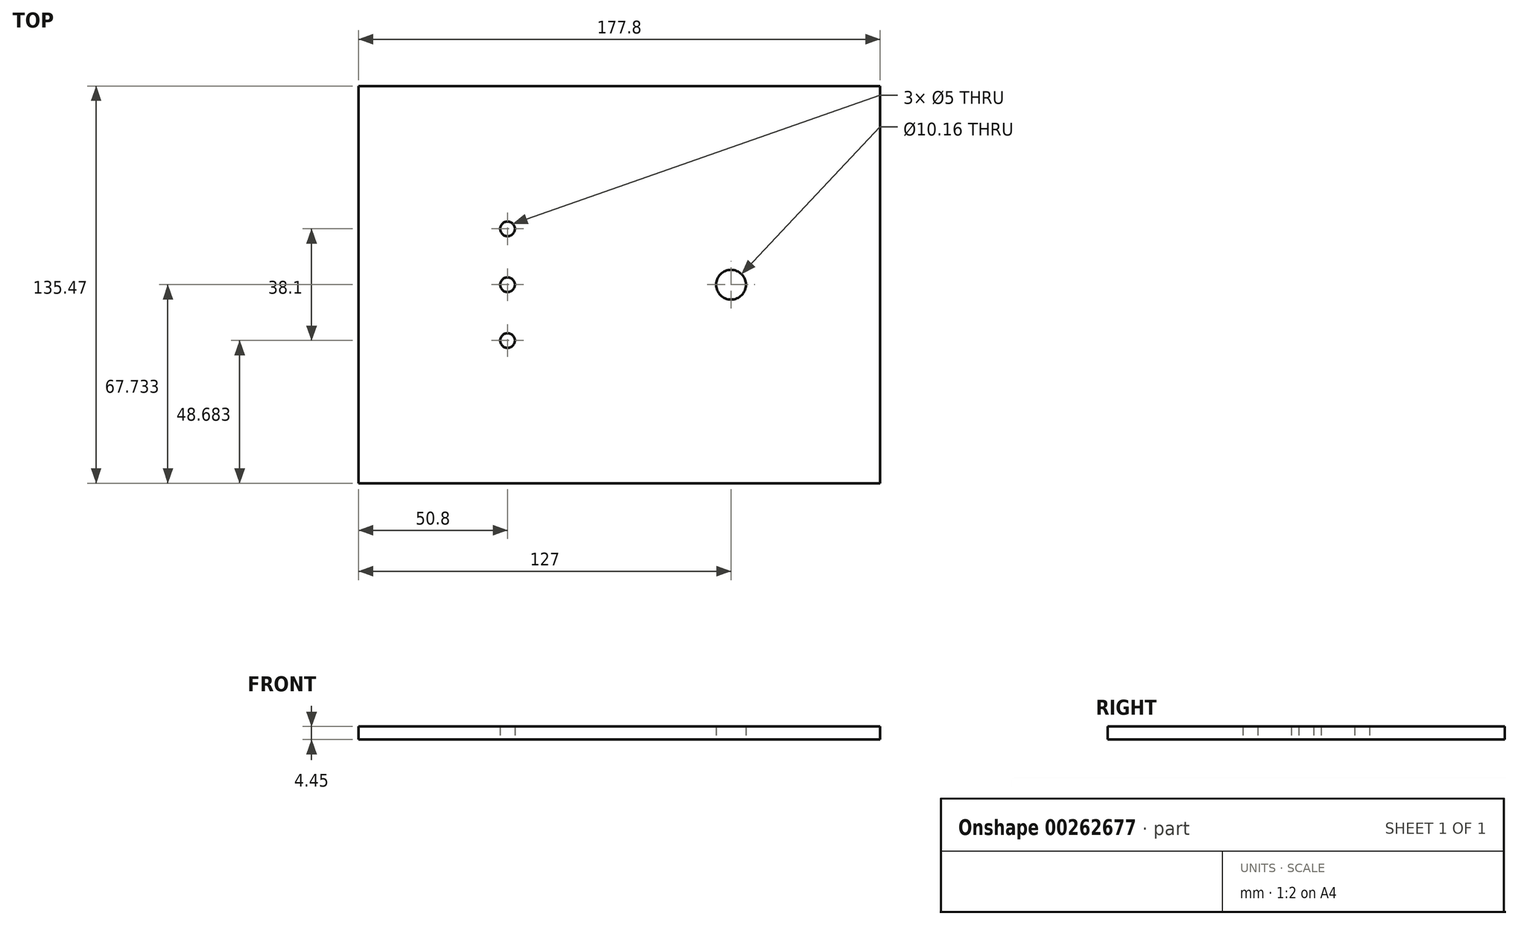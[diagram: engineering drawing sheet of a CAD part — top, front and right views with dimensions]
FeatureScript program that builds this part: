
annotation { "Feature Type Name" : "Feature", "Feature Type Description" : "" }
export const myFeature = defineFeature(function(context is Context, id is Id, definition is map)
    precondition{}
    {
        {
            var Q0;
            Q0=qCreatedBy(makeId("Top.planeOp"),FACE);
            var sketch = newSketch(context, id + "F0", { "sketchPlane" : qUnion([Q0])});
            skLineSegment(sketch, "E0.bottom", {"start": v(0, 0) * mm, "end": v(177.8, 0) * mm});
            skLineSegment(sketch, "E0.top", {"start": v(0, 135.47) * mm, "end": v(177.8, 135.47) * mm});
            skLineSegment(sketch, "E0.left", {"start": v(0, 0) * mm, "end": v(0, 135.47) * mm});
            skLineSegment(sketch, "E0.right", {"start": v(177.8, 0) * mm, "end": v(177.8, 135.47) * mm});
            skCircle(sketch, "E1", {"center": v(50.8, 86.78) * mm, "radius": 2.5 * mm});
            skCircle(sketch, "E2", {"center": v(50.8, 67.73) * mm, "radius": 2.5 * mm});
            skCircle(sketch, "E3", {"center": v(50.8, 48.68) * mm, "radius": 2.5 * mm});
            skCircle(sketch, "E4", {"center": v(127, 67.73) * mm, "radius": 5.08 * mm});
            skPoint(sketch, "E5", {"position": v(177.8, 67.73) * mm});
            skSolve(sketch);
        }
        {
            var Q0;
            Q0=makeQuery(id+"F0.imprint","IMPRINT",FACE,{"disambiguationData":[TD([[makeQuery(id+"F0.imprint","IMPRINT",EDGE,{"derivedFrom":sQuery(id+"F0.wireOp",EDGE,"E0.bottom")}),1.0]])]});
            extrude(context, id + "F1", {"entities" : qUnion([Q0]), "depth" : 4.44 * mm});
        }
    });
